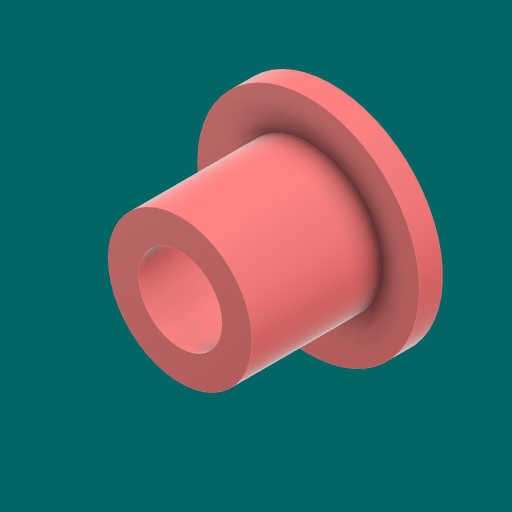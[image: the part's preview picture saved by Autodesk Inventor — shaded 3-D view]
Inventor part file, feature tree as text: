
AUTODESK INVENTOR PART (.ipt)
format: ipt  version: 2023.1 (Build 271208000, 208)  size: 331,776 bytes
history: native  units: in
note: dims shown in document units (in); Inventor stores cm internally (conversion verified against a paired STEP export)
features: extrude x2, sketch x2, chamfer x1
ambient origin geometry x8: Origin, YZ Plane, XZ Plane, XY Plane, X Axis, Y Axis, Z Axis, Center Point
bodies: Solid1 (feature_tree)
feature tree (5):
  extrude  "Extrusion1"  Depth=0.18in
  extrude  "Extrusion2"  Depth=0.05in
  chamfer  "Chamfer1"  Distance=0.05in
  sketch  "Sketch1"  dims[d0=0.3091in d1=0.18in]
  sketch  "Sketch2"  dims[d2=0.2756in d3=0.0in d4=0.4764in d5=0.05in d6=0.0in d7=0.0236in d8=0.125in d9=45.0deg]
